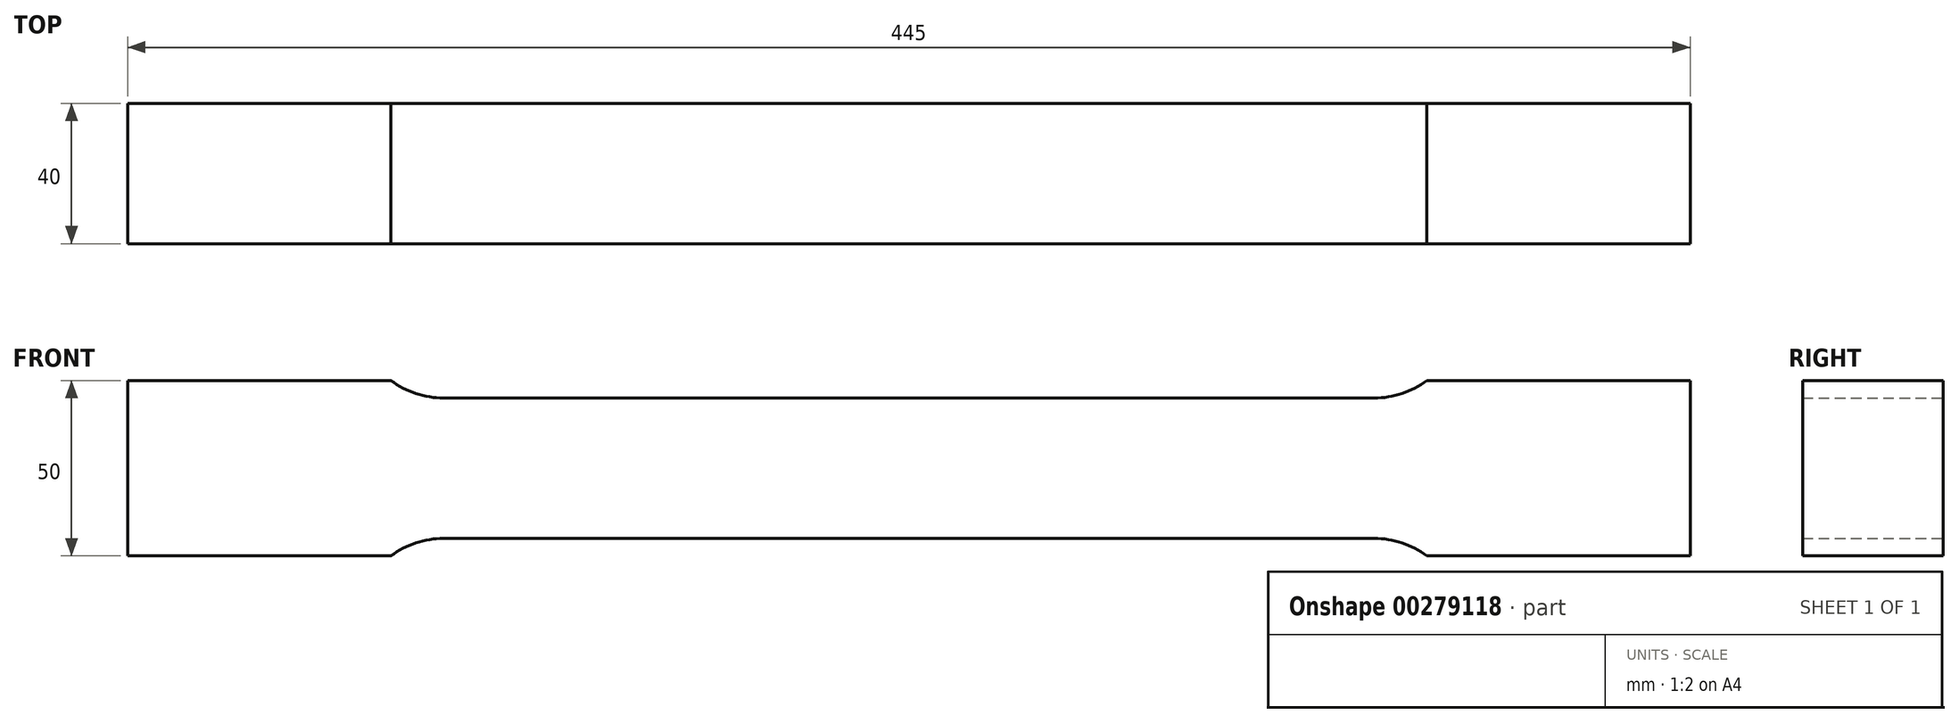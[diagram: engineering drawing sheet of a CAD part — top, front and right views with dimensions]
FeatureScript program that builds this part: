
annotation { "Feature Type Name" : "Feature", "Feature Type Description" : "" }
export const myFeature = defineFeature(function(context is Context, id is Id, definition is map)
    precondition{}
    {
        {
            var Q0;
            Q0=qCreatedBy(makeId("Front.planeOp"),FACE);
            var sketch = newSketch(context, id + "F0", { "sketchPlane" : qUnion([Q0])});
            skLineSegment(sketch, "E0", {"start": v(0, 20) * mm, "end": v(132.5, 20) * mm});
            skArc(sketch, "E1", {"start": v(132.5, 20) * mm, "mid": v(140.4, 21.28) * mm, "end": v(147.5, 25) * mm});
            skLineSegment(sketch, "E2", {"start": v(147.5, 25) * mm, "end": v(222.5, 25) * mm});
            skLineSegment(sketch, "E3", {"start": v(222.5, 25) * mm, "end": v(222.5, 0) * mm});
            skLineSegment(sketch, "E4.MirrorCS", {"start": v(222.5, -25) * mm, "end": v(222.5, 0) * mm});
            skLineSegment(sketch, "E5.MirrorCS", {"start": v(147.5, -25) * mm, "end": v(222.5, -25) * mm});
            skLineSegment(sketch, "E6.MirrorCS", {"start": v(0, -20) * mm, "end": v(132.5, -20) * mm});
            skArc(sketch, "E7.MirrorCS", {"start": v(132.5, -20) * mm, "mid": v(140.4, -21.28) * mm, "end": v(147.5, -25) * mm});
            skArc(sketch, "E8.MirrorCS", {"start": v(-132.5, -20) * mm, "mid": v(-140.4, -21.28) * mm, "end": v(-147.5, -25) * mm});
            skLineSegment(sketch, "E9.MirrorCS", {"start": v(0, -20) * mm, "end": v(-132.5, -20) * mm});
            skArc(sketch, "E10.MirrorCS", {"start": v(-132.5, 20) * mm, "mid": v(-140.4, 21.28) * mm, "end": v(-147.5, 25) * mm});
            skLineSegment(sketch, "E11.MirrorCS", {"start": v(-147.5, 25) * mm, "end": v(-222.5, 25) * mm});
            skLineSegment(sketch, "E12.MirrorCS", {"start": v(-147.5, -25) * mm, "end": v(-222.5, -25) * mm});
            skLineSegment(sketch, "E13.MirrorCS", {"start": v(-222.5, -25) * mm, "end": v(-222.5, 0) * mm});
            skLineSegment(sketch, "E14.MirrorCS", {"start": v(-222.5, 25) * mm, "end": v(-222.5, 0) * mm});
            skLineSegment(sketch, "E15.MirrorCS", {"start": v(0, 20) * mm, "end": v(-132.5, 20) * mm});
            skSolve(sketch);
        }
        {
            var Q0;
            Q0 = qSketchRegion(id + "F0", true);
            extrude(context, id + "F1", {"entities" : qUnion([Q0]), "endBound" : BoundingType.SYMMETRIC, "depth" : 40 * mm});
        }
    });
